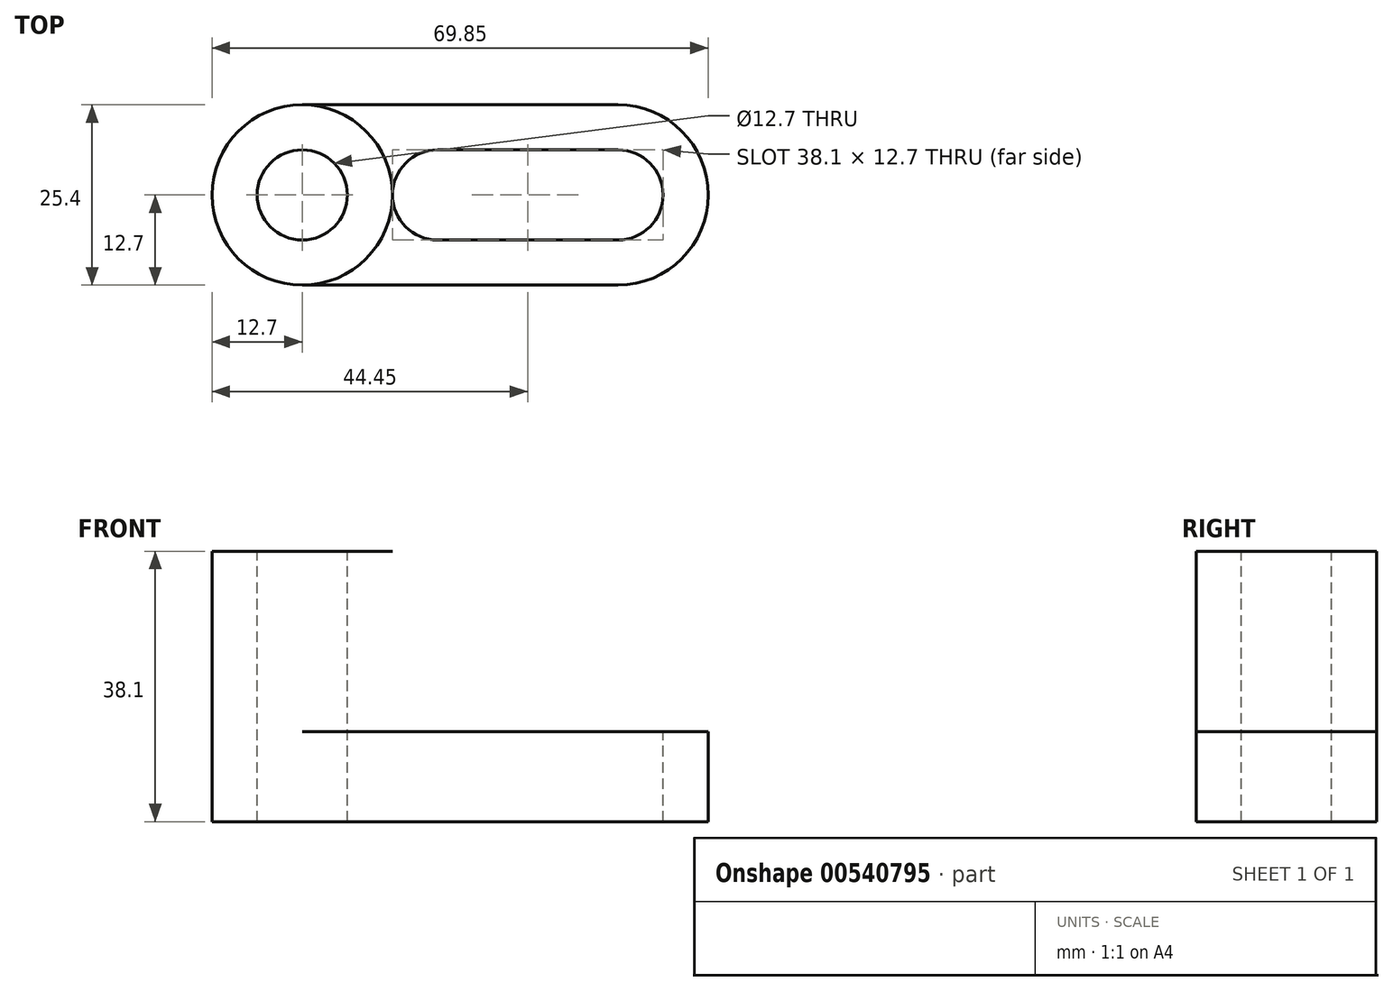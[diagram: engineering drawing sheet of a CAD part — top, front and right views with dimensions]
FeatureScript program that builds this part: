
annotation { "Feature Type Name" : "Feature", "Feature Type Description" : "" }
export const myFeature = defineFeature(function(context is Context, id is Id, definition is map)
    precondition{}
    {
        {
            var Q0;
            Q0=qCreatedBy(makeId("Front.planeOp"),FACE);
            var sketch = newSketch(context, id + "F0", { "sketchPlane" : qUnion([Q0])});
            skLineSegment(sketch, "E0", {"start": v(0, 0) * mm, "end": v(69.85, 0) * mm});
            skLineSegment(sketch, "E1", {"start": v(69.85, 0) * mm, "end": v(69.85, 12.7) * mm});
            skLineSegment(sketch, "E2", {"start": v(0, 12.7) * mm, "end": v(0, 0) * mm});
            skLineSegment(sketch, "E3", {"start": v(0, 12.7) * mm, "end": v(69.85, 12.7) * mm});
            skSolve(sketch);
        }
        {
            var Q0;
            Q0=makeQuery(id+"F0.imprint","IMPRINT",FACE,{"disambiguationData":[TD([[makeQuery(id+"F0.imprint","IMPRINT",EDGE,{"derivedFrom":sQuery(id+"F0.wireOp",EDGE,"E0")}),1.0]])]});
            extrude(context, id + "F1", {"entities" : qUnion([Q0]), "depth" : 25.4 * mm, "offsetDistance" : 25.4 * mm});
        }
        {
            var Q0;
            Q0=makeQuery(id+"F1.opExtrude","SWEPT_FACE",FACE,{"disambiguationData":[OSD([sQuery(id+"F0.wireOp",EDGE,"E3")])]});
            var sketch = newSketch(context, id + "F2", { "sketchPlane" : qUnion([Q0])});
            skCircle(sketch, "E4", {"center": v(57.15, -12.7) * mm, "radius": 6.35 * mm});
            skCircle(sketch, "E5", {"center": v(31.75, -12.7) * mm, "radius": 6.35 * mm});
            skLineSegment(sketch, "E6", {"start": v(31.75, -19.05) * mm, "end": v(57.15, -19.05) * mm});
            skLineSegment(sketch, "E7", {"start": v(31.75, -6.35) * mm, "end": v(57.15, -6.35) * mm});
            skSolve(sketch);
        }
        {
            var Q0;
            {var subQ0=sQuery(id+"F2.wireOp",EDGE,"E5");var subQ1=makeQuery(id+"F2.imprint","INTERSECT",VERTEX,{"derivedFrom":[subQ0,sQuery(id+"F2.wireOp",EDGE,"E6")]});Q0=makeQuery(id+"F2.imprint","IMPRINT",FACE,{"disambiguationData":[TD([[makeQuery(id+"F2.imprint","IMPRINT",EDGE,{"disambiguationData":[TD([[subQ1,1.0]])],"derivedFrom":subQ0}),1.0]])]});}
            var Q1;
            {var subQ0=sQuery(id+"F2.wireOp",EDGE,"E6");Q1=makeQuery(id+"F2.imprint","IMPRINT",FACE,{"disambiguationData":[TD([[makeQuery(id+"F2.imprint","IMPRINT",EDGE,{"derivedFrom":subQ0}),1.0]])]});}
            var Q2;
            {var subQ0=sQuery(id+"F2.wireOp",EDGE,"E4");var subQ1=makeQuery(id+"F2.imprint","INTERSECT",VERTEX,{"derivedFrom":[subQ0,sQuery(id+"F2.wireOp",EDGE,"E6")]});Q2=makeQuery(id+"F2.imprint","IMPRINT",FACE,{"disambiguationData":[TD([[makeQuery(id+"F2.imprint","IMPRINT",EDGE,{"disambiguationData":[TD([[subQ1,1.0]])],"derivedFrom":subQ0}),1.0]])]});}
            extrude(context, id + "F3", {"entities" : qUnion([Q0, Q1, Q2]), "operationType" : NewBodyOperationType.REMOVE, "oppositeDirection" : true, "depth" : 12.7 * mm, "offsetDistance" : 25.4 * mm});
        }
        {
            var Q0;
            Q0=makeQuery(id+"F1.opExtrude","SWEPT_FACE",FACE,{"disambiguationData":[OSD([sQuery(id+"F0.wireOp",EDGE,"E3")])]});
            var sketch = newSketch(context, id + "F4", { "sketchPlane" : qUnion([Q0])});
            skCircle(sketch, "E8", {"center": v(12.7, -12.7) * mm, "radius": 12.7 * mm});
            skPoint(sketch, "E8.centerSnap0", {"position": v(25.4, -12.7) * mm});
            skSolve(sketch);
        }
        {
            var Q0;
            {var subQ0=sQuery(id+"F4.wireOp",EDGE,"E8");var subQ1=sQuery(id+"F0.wireOp",EDGE,"E3");var subQ2=makeQuery(id+"F4.imprint","INTERSECT",VERTEX,{"derivedFrom":[makeQuery(id+"F1.opExtrude","CAP_EDGE",EDGE,{"disambiguationData":[OSD([subQ1])],"isStart":true}),subQ0]});Q0=makeQuery(id+"F4.imprint","IMPRINT",FACE,{"disambiguationData":[TD([[makeQuery(id+"F4.imprint","IMPRINT",EDGE,{"disambiguationData":[TD([[subQ2,1.0]])],"derivedFrom":subQ0}),1.0]])]});}
            extrude(context, id + "F5", {"entities" : qUnion([Q0]), "operationType" : NewBodyOperationType.ADD, "depth" : 25.4 * mm, "offsetDistance" : 25.4 * mm});
        }
        {
            var Q0;
            {var subQ0=sQuery(id+"F0.wireOp",EDGE,"E3");var subQ1=sQuery(id+"F0.wireOp",EDGE,"E2");var subQ2=makeQuery(id+"F1.opExtrude","SWEPT_FACE",FACE,{"disambiguationData":[OSD([subQ0])]});Q0=makeQuery(id+"F5.boolean.opBoolean","SPLIT",FACE,{"disambiguationData":[TD([makeQuery(id+"F1.opExtrude","CAP_FACE",FACE,{"disambiguationData":[OSD([sQuery(id+"F0.wireOp",EDGE,"E0"),sQuery(id+"F0.wireOp",EDGE,"E1"),subQ1,subQ0])],"isStart":true}),makeQuery(id+"F1.opExtrude","SWEPT_FACE",FACE,{"disambiguationData":[OSD([subQ1])]}),subQ2,makeQuery(id+"F5.opExtrude","SWEPT_FACE",FACE,{"disambiguationData":[OSD([sQuery(id+"F4.wireOp",EDGE,"E8")])]})])],"derivedFrom":subQ2});}
            var Q1;
            {var subQ0=sQuery(id+"F0.wireOp",EDGE,"E3");var subQ1=sQuery(id+"F0.wireOp",EDGE,"E2");var subQ2=makeQuery(id+"F1.opExtrude","SWEPT_FACE",FACE,{"disambiguationData":[OSD([subQ0])]});Q1=makeQuery(id+"F5.boolean.opBoolean","SPLIT",FACE,{"disambiguationData":[TD([makeQuery(id+"F1.opExtrude","CAP_FACE",FACE,{"disambiguationData":[OSD([sQuery(id+"F0.wireOp",EDGE,"E0"),sQuery(id+"F0.wireOp",EDGE,"E1"),subQ1,subQ0])],"isStart":false}),makeQuery(id+"F1.opExtrude","SWEPT_FACE",FACE,{"disambiguationData":[OSD([subQ1])]}),subQ2,makeQuery(id+"F5.opExtrude","SWEPT_FACE",FACE,{"disambiguationData":[OSD([sQuery(id+"F4.wireOp",EDGE,"E8")])]})])],"derivedFrom":subQ2});}
            extrude(context, id + "F6", {"entities" : qUnion([Q0, Q1]), "operationType" : NewBodyOperationType.REMOVE, "oppositeDirection" : true, "depth" : 12.7 * mm, "offsetDistance" : 25.4 * mm});
        }
        {
            var Q0;
            Q0=makeQuery(id+"F5.opExtrude","CAP_FACE",FACE,{"disambiguationData":[OSD([sQuery(id+"F4.wireOp",EDGE,"E8")])],"isStart":false});
            var sketch = newSketch(context, id + "F7", { "sketchPlane" : qUnion([Q0])});
            skCircle(sketch, "E9", {"center": v(12.7, -12.7) * mm, "radius": 6.35 * mm});
            skSolve(sketch);
        }
        {
            var Q0;
            Q0=makeQuery(id+"F7.imprint","IMPRINT",FACE,{"disambiguationData":[TD([[makeQuery(id+"F7.imprint","IMPRINT",EDGE,{"derivedFrom":sQuery(id+"F7.wireOp",EDGE,"E9")}),1.0]])]});
            extrude(context, id + "F8", {"entities" : qUnion([Q0]), "operationType" : NewBodyOperationType.REMOVE, "oppositeDirection" : true, "depth" : 38.1 * mm, "offsetDistance" : 25.4 * mm});
        }
        {
            var Q0;
            {var subQ0=sQuery(id+"F0.wireOp",EDGE,"E3");var subQ1=makeQuery(id+"F1.opExtrude","SWEPT_FACE",FACE,{"disambiguationData":[OSD([subQ0])]});var subQ2=sQuery(id+"F0.wireOp",EDGE,"E1");var subQ3=sQuery(id+"F0.wireOp",EDGE,"E2");var subQ4=sQuery(id+"F0.wireOp",EDGE,"E0");Q0=makeQuery(id+"F5.boolean.opBoolean","SPLIT",FACE,{"disambiguationData":[TD([makeQuery(id+"F1.opExtrude","CAP_FACE",FACE,{"disambiguationData":[OSD([subQ4,subQ2,subQ3,subQ0])],"isStart":true}),makeQuery(id+"F1.opExtrude","CAP_FACE",FACE,{"disambiguationData":[OSD([subQ4,subQ2,subQ3,subQ0])],"isStart":false}),makeQuery(id+"F1.opExtrude","SWEPT_FACE",FACE,{"disambiguationData":[OSD([subQ2])]}),subQ1,makeQuery(id+"F3.boolean.opBoolean","COPY",FACE,{"derivedFrom":makeQuery(id+"F3.opExtrude","SWEPT_FACE",FACE,{"disambiguationData":[OSD([sQuery(id+"F2.wireOp",EDGE,"E4")])]})}),makeQuery(id+"F3.boolean.opBoolean","COPY",FACE,{"derivedFrom":makeQuery(id+"F3.opExtrude","SWEPT_FACE",FACE,{"disambiguationData":[OSD([sQuery(id+"F2.wireOp",EDGE,"E5")])]})}),makeQuery(id+"F3.boolean.opBoolean","COPY",FACE,{"derivedFrom":makeQuery(id+"F3.opExtrude","SWEPT_FACE",FACE,{"disambiguationData":[OSD([sQuery(id+"F2.wireOp",EDGE,"E6")])]})}),makeQuery(id+"F3.boolean.opBoolean","COPY",FACE,{"derivedFrom":makeQuery(id+"F3.opExtrude","SWEPT_FACE",FACE,{"disambiguationData":[OSD([sQuery(id+"F2.wireOp",EDGE,"E7")])]})}),makeQuery(id+"F5.opExtrude","SWEPT_FACE",FACE,{"disambiguationData":[OSD([sQuery(id+"F4.wireOp",EDGE,"E8")])]})])],"derivedFrom":subQ1});}
            var sketch = newSketch(context, id + "F9", { "sketchPlane" : qUnion([Q0])});
            skArc(sketch, "E10", {"start": v(57.15, -25.4) * mm, "mid": v(69.85, -12.7) * mm, "end": v(57.15, 0) * mm});
            skSolve(sketch);
        }
        {
            var Q0;
            {var subQ0=sQuery(id+"F9.wireOp",EDGE,"E10");var subQ1=sQuery(id+"F0.wireOp",EDGE,"E3");var subQ2=sQuery(id+"F0.wireOp",EDGE,"E1");var subQ5=makeQuery(id+"F1.opExtrude","SWEPT_EDGE",EDGE,{"disambiguationData":[OSD([subQ2,subQ1])]});var subQ6=makeQuery(id+"F9.imprint","INTERSECT",VERTEX,{"derivedFrom":[subQ5,subQ0]});Q0=makeQuery(id+"F9.imprint","IMPRINT",FACE,{"disambiguationData":[TD([[makeQuery(id+"F9.imprint","IMPRINT",EDGE,{"disambiguationData":[TD([[subQ6,-1.0]])],"derivedFrom":subQ0}),-1.0]])]});}
            var Q1;
            {var subQ0=sQuery(id+"F9.wireOp",EDGE,"E10");var subQ1=sQuery(id+"F0.wireOp",EDGE,"E3");var subQ2=sQuery(id+"F0.wireOp",EDGE,"E1");var subQ5=makeQuery(id+"F1.opExtrude","SWEPT_EDGE",EDGE,{"disambiguationData":[OSD([subQ2,subQ1])]});var subQ6=makeQuery(id+"F9.imprint","INTERSECT",VERTEX,{"derivedFrom":[subQ5,subQ0]});Q1=makeQuery(id+"F9.imprint","IMPRINT",FACE,{"disambiguationData":[TD([[makeQuery(id+"F9.imprint","IMPRINT",EDGE,{"disambiguationData":[TD([[subQ6,1.0]])],"derivedFrom":subQ0}),-1.0]])]});}
            extrude(context, id + "F10", {"entities" : qUnion([Q0, Q1]), "operationType" : NewBodyOperationType.REMOVE, "oppositeDirection" : true, "depth" : 12.7 * mm, "offsetDistance" : 25.4 * mm});
        }
    });
